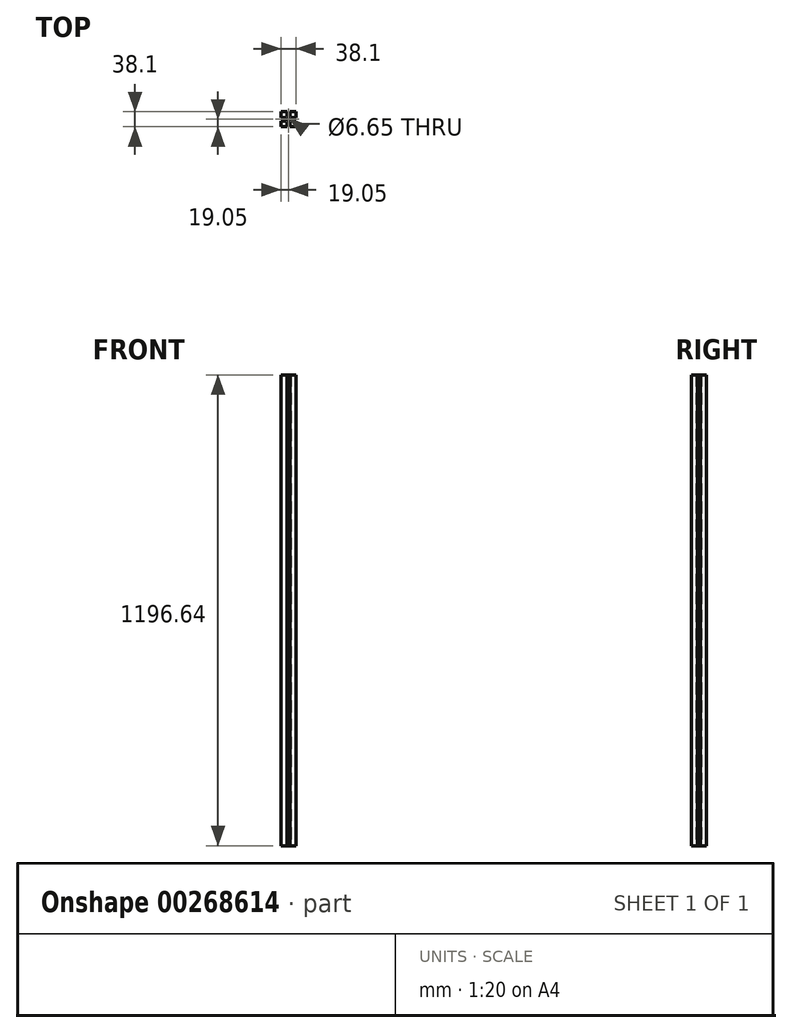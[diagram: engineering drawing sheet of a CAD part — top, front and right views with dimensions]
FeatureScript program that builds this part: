
annotation { "Feature Type Name" : "Feature", "Feature Type Description" : "" }
export const myFeature = defineFeature(function(context is Context, id is Id, definition is map)
    precondition{}
    {
        {
            var Q0;
            Q0=qCreatedBy(makeId("Top.planeOp"),FACE);
            var sketch = newSketch(context, id + "F0", { "sketchPlane" : qUnion([Q0])});
            skPoint(sketch, "E0.middle", {"position": v(0, 0) * mm});
            skCircle(sketch, "E1", {"center": v(0, 0) * mm, "radius": 3.33 * mm});
            skLineSegment(sketch, "E2.top", {"start": v(4.06, 6.76) * mm, "end": v(-4.06, 6.76) * mm});
            skLineSegment(sketch, "E2.left", {"start": v(6.76, -4.06) * mm, "end": v(6.76, 4.06) * mm});
            skLineSegment(sketch, "E2.right", {"start": v(-6.76, -4.06) * mm, "end": v(-6.76, 4.06) * mm});
            skLineSegment(sketch, "E3", {"start": v(-4.06, 19.05) * mm, "end": v(-4.06, 6.76) * mm});
            skLineSegment(sketch, "E4", {"start": v(4.06, 19.05) * mm, "end": v(4.06, 6.76) * mm});
            skLineSegment(sketch, "E5", {"start": v(-19.05, 4.06) * mm, "end": v(-6.76, 4.06) * mm});
            skLineSegment(sketch, "E6.MirrorCS", {"start": v(-19.05, -4.06) * mm, "end": v(-6.76, -4.06) * mm});
            skLineSegment(sketch, "E7", {"start": v(-19.05, 4.06) * mm, "end": v(-19.05, 19.05) * mm});
            skLineSegment(sketch, "E8", {"start": v(-19.05, 19.05) * mm, "end": v(-4.06, 19.05) * mm});
            skLineSegment(sketch, "E9", {"start": v(4.06, 19.05) * mm, "end": v(19.05, 19.05) * mm});
            skLineSegment(sketch, "E10", {"start": v(19.05, 19.05) * mm, "end": v(19.05, 4.06) * mm});
            skLineSegment(sketch, "E11", {"start": v(-19.05, -4.06) * mm, "end": v(-19.05, -19.05) * mm});
            skLineSegment(sketch, "E12", {"start": v(-19.05, -19.05) * mm, "end": v(-4.06, -19.05) * mm});
            skLineSegment(sketch, "E13", {"start": v(4.06, -19.05) * mm, "end": v(19.05, -19.05) * mm});
            skLineSegment(sketch, "E14", {"start": v(19.05, -19.05) * mm, "end": v(19.05, -4.06) * mm});
            skLineSegment(sketch, "E15.trimOffspring", {"start": v(6.76, 4.06) * mm, "end": v(19.05, 4.06) * mm});
            skLineSegment(sketch, "E16.trimOffspring", {"start": v(6.76, -4.06) * mm, "end": v(19.05, -4.06) * mm});
            skLineSegment(sketch, "E17", {"start": v(-4.06, -19.05) * mm, "end": v(-4.06, -6.76) * mm});
            skLineSegment(sketch, "E18", {"start": v(-4.06, -6.76) * mm, "end": v(4.06, -6.76) * mm});
            skLineSegment(sketch, "E19", {"start": v(4.06, -6.76) * mm, "end": v(4.06, -19.05) * mm});
            skSolve(sketch);
        }
        {
            var Q0;
            Q0=qSketchRegion(id+"F0",true);
            extrude(context, id + "F1", {"entities" : qUnion([Q0]), "depth" : 1196.64 * mm});
        }
    });
